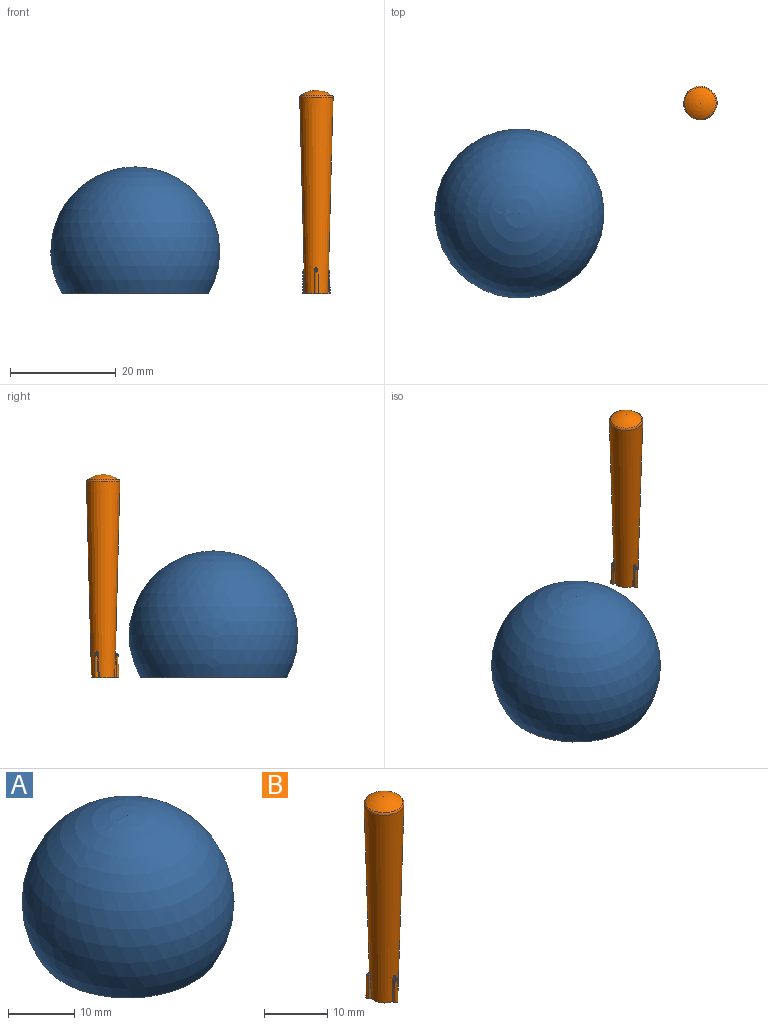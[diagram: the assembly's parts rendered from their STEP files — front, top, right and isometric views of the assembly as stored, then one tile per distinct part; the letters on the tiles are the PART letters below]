
ASSEMBLY  parts=2 mates=1
PART A: 42 faces, bbox 32x32x25.7 mm
  f0: cone r=3.75mm half-angle=3deg, axis (0,0,1), area 9.2mm2, adj f3,f15,f16,f23,f32,f40
  f1: cone r=3.75mm half-angle=3deg, axis (0,0,1), area 9.2mm2, adj f4,f13,f14,f29,f38,f41
  f2: cone r=3.75mm half-angle=3deg, axis (0,0,1), area 9.2mm2, adj f5,f12,f17,f26,f35,f39
  f3: plane 3.49x2.03mm, normal (0,0,-1), area 0.9mm2, adj f0,f19,f23,f32
  f4: plane 4.03x0.75mm, normal (0,0,-1), area 0.9mm2, adj f1,f20,f29,f38
  f5: plane 3.49x2.03mm, normal (0,0,-1), area 0.9mm2, adj f2,f18,f26,f35
  f6: cone r=2.33mm half-angle=1deg, axis (0,0,-1), area 9.2mm2, adj f11,f19,f21,f30
  f7: cone r=2.33mm half-angle=1deg, axis (0,0,-1), area 9.2mm2, adj f11,f20,f27,f36
  f8: cone r=2.33mm half-angle=1deg, axis (0,0,-1), area 9.2mm2, adj f11,f18,f24,f33
  f9: sphere r=16mm, area 2412.7mm2, adj f10
  f10: plane 27.71x27.71mm, normal (0,0,-1), area 116.1mm2, adj f9,f11
  f11: sphere r=14.8mm, area 2011.1mm2, adj f6,f7,f8,f10,f12,f13,f14,f15
  f12: plane 3.42x3.14mm, normal (0.5,0.87,0), area 4.2mm2, adj f2,f11,f33,f35,f39
  f13: plane 3.42x3.14mm, normal (-0.5,-0.87,0), area 4.2mm2, adj f1,f11,f36,f38,f41
  f14: plane 3.42x3.14mm, normal (0.5,-0.87,0), area 4.2mm2, adj f1,f11,f27,f29,f41
  f15: plane 3.42x3.14mm, normal (-0.5,0.87,0), area 4.2mm2, adj f0,f11,f30,f32,f40
  f16: plane 3.62x3.42mm, normal (-1,0,0), area 4.2mm2, adj f0,f11,f21,f23,f40
  f17: plane 3.62x3.42mm, normal (1,0,0), area 4.2mm2, adj f2,f11,f24,f26,f39
  f18: torus R=3.31mm, axis (0,0,1), area 4.8mm2, adj f5,f8,f25,f34
  f19: torus R=3.31mm, axis (0,0,1), area 4.8mm2, adj f3,f6,f22,f31
  f20: torus R=3.31mm, axis (0,0,1), area 4.8mm2, adj f4,f7,f28,f37
  f21: bspline ~7.61x1.03mm, area 3.8mm2, adj f6,f11,f16,f22
  f22: sphere r=1mm, area 1.2mm2, adj f19,f21,f23
  f23: cylinder r=1mm len=1mm, axis (0,1,0), area 0.7mm2, adj f0,f3,f16,f22
  f24: bspline ~7.61x1.03mm, area 3.8mm2, adj f8,f11,f17,f25
  f25: sphere r=1mm, area 1.5mm2, adj f18,f24,f26
  f26: cylinder r=1mm len=1mm, axis (0,-1,0), area 0.7mm2, adj f2,f5,f17,f25
  f27: bspline ~10.86x1.21mm, area 3.8mm2, adj f7,f11,f14,f28
  f28: sphere r=1mm, area 1.2mm2, adj f20,f27,f29
  f29: cylinder r=1mm len=1.16mm, axis (-0.87,-0.5,0), area 0.7mm2, adj f1,f4,f14,f28
  f30: bspline ~7.61x0.98mm, area 3.8mm2, adj f6,f11,f15,f31
  f31: sphere r=1mm, area 1.2mm2, adj f19,f30,f32
  f32: cylinder r=1mm len=1.16mm, axis (0.87,0.5,0), area 0.7mm2, adj f0,f3,f15,f31
  f33: bspline ~10.86x1.01mm, area 3.8mm2, adj f8,f11,f12,f34
  f34: sphere r=1mm, area 1.2mm2, adj f18,f33,f35
  f35: cylinder r=1mm len=1.16mm, axis (0.87,-0.5,0), area 0.7mm2, adj f2,f5,f12,f34
  f36: bspline ~10.86x1.21mm, area 3.8mm2, adj f7,f11,f13,f37
  f37: sphere r=1mm, area 1.2mm2, adj f20,f36,f38
  f38: cylinder r=1mm len=1.16mm, axis (-0.87,0.5,0), area 0.7mm2, adj f1,f4,f13,f37
  f39: torus R=5.6mm, axis (0,0,-1), area 35.3mm2, adj f2,f11,f12,f17
  f40: torus R=5.6mm, axis (0,0,-1), area 35.3mm2, adj f0,f11,f15,f16
  f41: torus R=5.6mm, axis (0,0,-1), area 35.3mm2, adj f1,f11,f13,f14
PART B: 37 faces, bbox 6.9x6.9x38.5 mm
  f0: cone r=0.38mm half-angle=1deg, axis (0,0,-1), area 4.5mm2, adj f4,f7,f8,f21,f24
  f1: cone r=0.38mm half-angle=1deg, axis (0,0,-1), area 4.5mm2, adj f4,f9,f10,f27,f30
  f2: cone r=0.38mm half-angle=1deg, axis (0,0,-1), area 4.5mm2, adj f4,f11,f12,f33,f36
  f3: cone r=2.2mm half-angle=1.5deg, axis (0,0,1), area 616.7mm2, adj f4,f6,f7,f8,f9,f10,f11,f12
  f4: plane 5.21x5.15mm, normal (0,0,-1), area 16.7mm2, adj f0,f1,f2,f3,f7,f8,f9,f10
  f5: sphere r=5mm, area 30.7mm2, adj f6
  f6: torus R=2.67mm, axis (0,0,-1), area 9.4mm2, adj f3,f5
  f7: plane 4.54x0.41mm, normal (1,0,0.02), area 1.5mm2, adj f0,f3,f4,f19,f20
  f8: plane 4.54x0.41mm, normal (-1,0,0.02), area 1.5mm2, adj f0,f3,f4,f22,f23
  f9: plane 4.54x0.36mm, normal (-0.5,-0.87,0.02), area 1.5mm2, adj f1,f3,f4,f25,f26
  f10: plane 4.54x0.39mm, normal (0.5,0.87,0.02), area 1.5mm2, adj f1,f3,f4,f28,f29
  f11: plane 4.54x0.36mm, normal (0.5,-0.87,0.02), area 1.5mm2, adj f2,f3,f4,f31,f32
  f12: plane 4.54x0.39mm, normal (-0.5,0.87,0.02), area 1.5mm2, adj f2,f3,f4,f34,f35
  f13: torus R=2.83mm, axis (0,0,1), area 0.1mm2, adj f3,f14,f31,f34
  f14: torus R=2.38mm, axis (0,0,1), area 0.1mm2, adj f13,f32,f33,f35,f36
  f15: torus R=2.83mm, axis (0,0,1), area 0.1mm2, adj f3,f16,f25,f28
  f16: torus R=2.38mm, axis (0,0,1), area 0.1mm2, adj f15,f26,f27,f29,f30
  f17: torus R=2.38mm, axis (0,0,1), area 0.1mm2, adj f18,f20,f21,f23,f24
  f18: torus R=2.83mm, axis (0,0,1), area 0.1mm2, adj f3,f17,f19,f22
  f19: bspline ~0.77x0.58mm, area 0.1mm2, adj f3,f7,f18,f20
  f20: bspline ~0.28x0.27mm, area 0mm2, adj f7,f17,f19,f21
  f21: bspline ~0.42x0.38mm, area 0.1mm2, adj f0,f17,f20
  f22: bspline ~0.77x0.55mm, area 0.1mm2, adj f3,f8,f18,f23
  f23: bspline ~0.28x0.27mm, area 0mm2, adj f8,f17,f22,f24
  f24: bspline ~0.38x0.33mm, area 0.1mm2, adj f0,f17,f23
  f25: bspline ~0.77x0.51mm, area 0.1mm2, adj f3,f9,f15,f26
  f26: bspline ~0.31x0.29mm, area 0mm2, adj f9,f16,f25,f27
  f27: bspline ~0.44x0.42mm, area 0.1mm2, adj f1,f16,f26
  f28: bspline ~0.77x0.57mm, area 0.1mm2, adj f3,f10,f15,f29
  f29: bspline ~0.34x0.28mm, area 0mm2, adj f10,f16,f28,f30
  f30: bspline ~0.43x0.38mm, area 0.1mm2, adj f1,f16,f29
  f31: bspline ~0.77x0.48mm, area 0.1mm2, adj f3,f11,f13,f32
  f32: bspline ~0.31x0.29mm, area 0mm2, adj f11,f14,f31,f33
  f33: bspline ~0.42x0.38mm, area 0.1mm2, adj f2,f14,f32
  f34: bspline ~0.77x0.6mm, area 0.1mm2, adj f3,f12,f13,f35
  f35: bspline ~0.34x0.28mm, area 0mm2, adj f12,f14,f34,f36
  f36: bspline ~0.48x0.42mm, area 0.1mm2, adj f2,f14,f35
PLACE A t=(1.69,11.54,-6.05)mm
PLACE B t=(35.95,32.4,-6.05)mm
MATE planar A.f0 <-> B.f3  axis (0,0,-1) through (1.69,11.54,-6.05)mm
